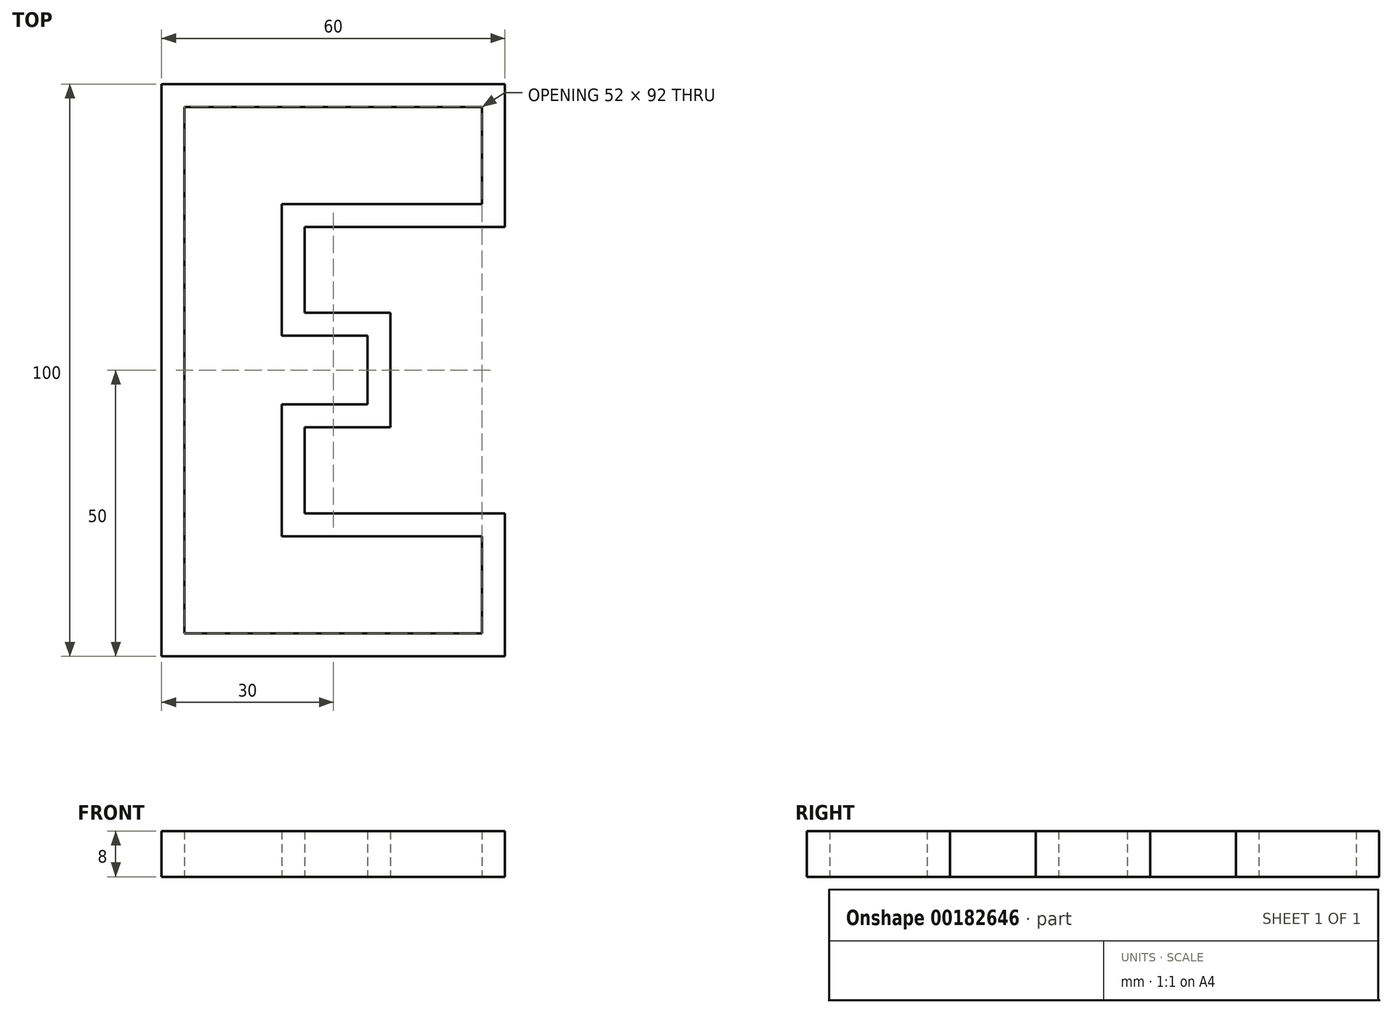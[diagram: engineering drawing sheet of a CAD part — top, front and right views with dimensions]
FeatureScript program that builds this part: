
annotation { "Feature Type Name" : "Feature", "Feature Type Description" : "" }
export const myFeature = defineFeature(function(context is Context, id is Id, definition is map)
    precondition{}
    {
        {
            var Q0;
            Q0=qCreatedBy(makeId("Top.planeOp"),FACE);
            var sketch = newSketch(context, id + "F0", { "sketchPlane" : qUnion([Q0])});
            skLineSegment(sketch, "E0", {"start": v(0, 0) * mm, "end": v(0, -50) * mm});
            skLineSegment(sketch, "E1", {"start": v(0, -50) * mm, "end": v(60, -50) * mm});
            skLineSegment(sketch, "E2", {"start": v(60, -50) * mm, "end": v(60, -25) * mm});
            skLineSegment(sketch, "E3", {"start": v(60, -25) * mm, "end": v(25, -25) * mm});
            skLineSegment(sketch, "E4", {"start": v(25, -25) * mm, "end": v(25, -10) * mm});
            skLineSegment(sketch, "E5", {"start": v(25, -10) * mm, "end": v(40, -10) * mm});
            skLineSegment(sketch, "E6", {"start": v(40, -10) * mm, "end": v(40, 0) * mm});
            skLineSegment(sketch, "E7.MirrorCS", {"start": v(0, 0) * mm, "end": v(0, 50) * mm});
            skLineSegment(sketch, "E8.MirrorCS", {"start": v(40, 10) * mm, "end": v(40, 0) * mm});
            skLineSegment(sketch, "E9.MirrorCS", {"start": v(25, 10) * mm, "end": v(40, 10) * mm});
            skLineSegment(sketch, "E10.MirrorCS", {"start": v(25, 25) * mm, "end": v(25, 10) * mm});
            skLineSegment(sketch, "E11.MirrorCS", {"start": v(60, 25) * mm, "end": v(25, 25) * mm});
            skLineSegment(sketch, "E12.MirrorCS", {"start": v(0, 50) * mm, "end": v(60, 50) * mm});
            skLineSegment(sketch, "E13.MirrorCS", {"start": v(60, 50) * mm, "end": v(60, 25) * mm});
            skLineSegment(sketch, "E14.0", {"start": v(4, 0) * mm, "end": v(4, -46) * mm});
            skLineSegment(sketch, "E14.1", {"start": v(4, -46) * mm, "end": v(56, -46) * mm});
            skLineSegment(sketch, "E14.2", {"start": v(56, -46) * mm, "end": v(56, -29) * mm});
            skLineSegment(sketch, "E14.3", {"start": v(21, 29) * mm, "end": v(21, 6) * mm});
            skLineSegment(sketch, "E14.4", {"start": v(56, 29) * mm, "end": v(21, 29) * mm});
            skLineSegment(sketch, "E14.5", {"start": v(56, 46) * mm, "end": v(56, 29) * mm});
            skLineSegment(sketch, "E14.6", {"start": v(4, 46) * mm, "end": v(56, 46) * mm});
            skLineSegment(sketch, "E14.7", {"start": v(21, 6) * mm, "end": v(36, 6) * mm});
            skLineSegment(sketch, "E14.8", {"start": v(36, 6) * mm, "end": v(36, 0) * mm});
            skLineSegment(sketch, "E14.9", {"start": v(36, -6) * mm, "end": v(36, 0) * mm});
            skLineSegment(sketch, "E14.10", {"start": v(4, 0) * mm, "end": v(4, 46) * mm});
            skLineSegment(sketch, "E14.11", {"start": v(21, -6) * mm, "end": v(36, -6) * mm});
            skLineSegment(sketch, "E14.12", {"start": v(21, -29) * mm, "end": v(21, -6) * mm});
            skLineSegment(sketch, "E14.13", {"start": v(56, -29) * mm, "end": v(21, -29) * mm});
            skSolve(sketch);
        }
        {
            var Q0;
            Q0 = qSketchRegion(id + "F0", true);
            extrude(context, id + "F1", {"entities" : qUnion([Q0]), "depth" : 8 * mm});
        }
    });
